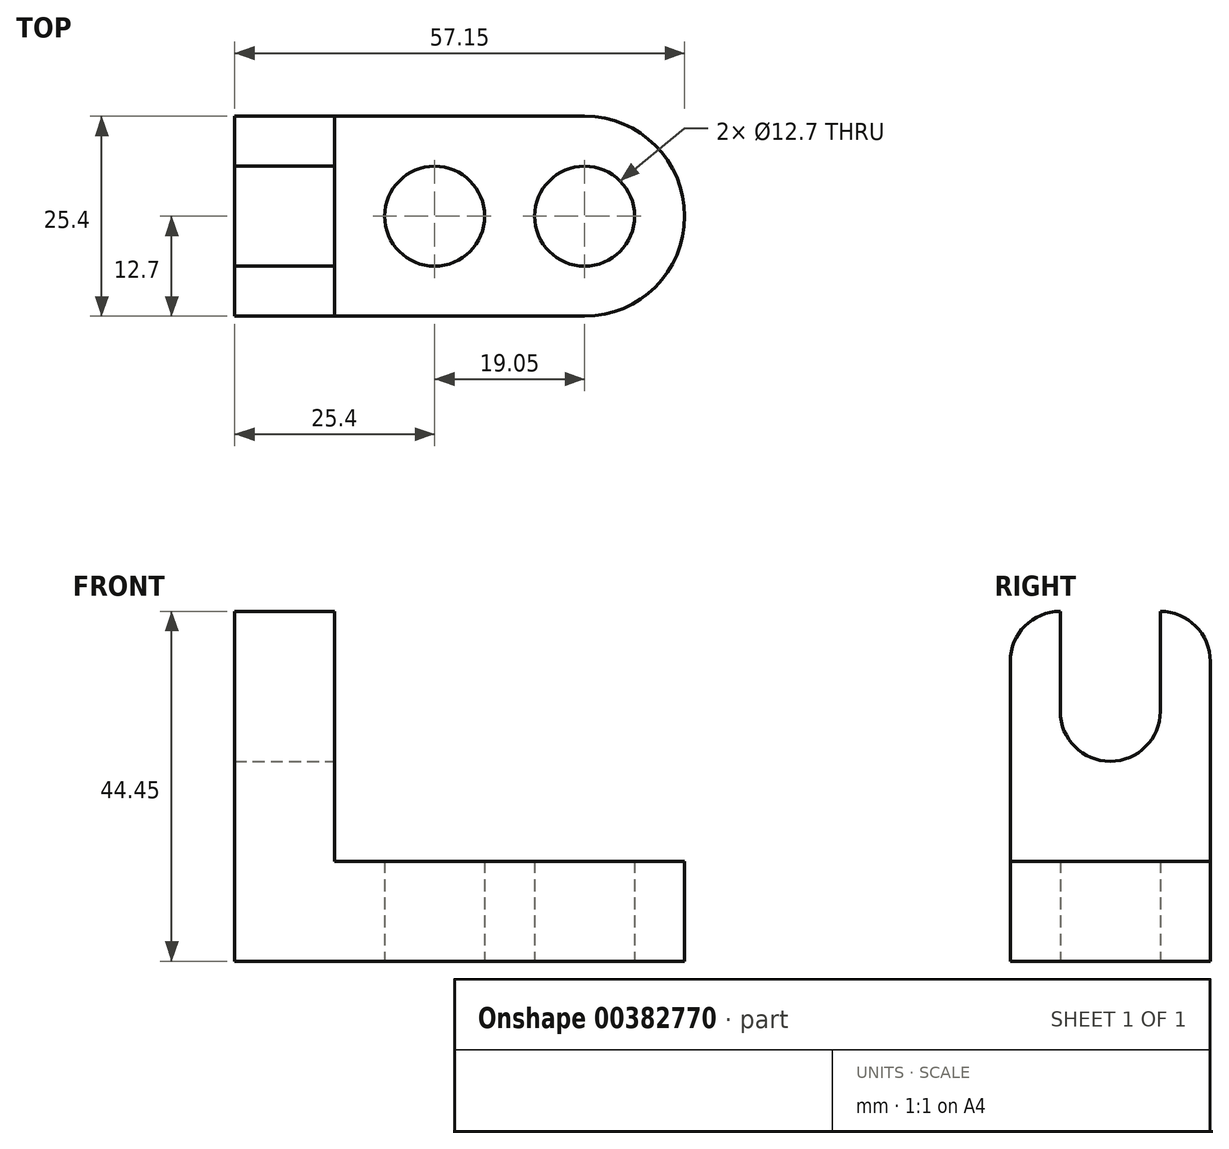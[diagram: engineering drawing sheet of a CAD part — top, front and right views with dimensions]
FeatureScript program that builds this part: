
annotation { "Feature Type Name" : "Feature", "Feature Type Description" : "" }
export const myFeature = defineFeature(function(context is Context, id is Id, definition is map)
    precondition{}
    {
        {
            var Q0;
            Q0=qCreatedBy(makeId("Front.planeOp"),FACE);
            var sketch = newSketch(context, id + "F0", { "sketchPlane" : qUnion([Q0])});
            skLineSegment(sketch, "E0", {"start": v(0, 0) * mm, "end": v(-57.15, 0) * mm});
            skLineSegment(sketch, "E1", {"start": v(-57.15, 0) * mm, "end": v(-57.15, 44.45) * mm});
            skLineSegment(sketch, "E2", {"start": v(-57.15, 44.45) * mm, "end": v(-44.45, 44.45) * mm});
            skLineSegment(sketch, "E3", {"start": v(-44.45, 44.45) * mm, "end": v(-44.45, 12.7) * mm});
            skLineSegment(sketch, "E4", {"start": v(-44.45, 12.7) * mm, "end": v(0, 12.7) * mm});
            skLineSegment(sketch, "E5", {"start": v(0, 12.7) * mm, "end": v(0, 0) * mm});
            skSolve(sketch);
        }
        {
            var Q0;
            Q0 = qSketchRegion(id + "F0", true);
            extrude(context, id + "F1", {"entities" : qUnion([Q0]), "depth" : 25.4 * mm});
        }
        {
            var Q0;
            Q0=qCreatedBy(makeId("Top.planeOp"),FACE);
            var sketch = newSketch(context, id + "F2", { "sketchPlane" : qUnion([Q0])});
            skCircle(sketch, "E6", {"center": v(-31.75, -12.7) * mm, "radius": 6.35 * mm});
            skCircle(sketch, "E7", {"center": v(-12.7, -12.7) * mm, "radius": 6.35 * mm});
            skArc(sketch, "E8", {"start": v(0, -12.7) * mm, "mid": v(-3.72, -3.72) * mm, "end": v(-12.7, 0) * mm});
            skArc(sketch, "E9", {"start": v(-12.7, -25.4) * mm, "mid": v(-3.72, -21.68) * mm, "end": v(0, -12.7) * mm});
            skLineSegment(sketch, "E10", {"start": v(-12.7, 0) * mm, "end": v(0, 0) * mm});
            skLineSegment(sketch, "E11", {"start": v(0, 0) * mm, "end": v(0, -12.7) * mm});
            skLineSegment(sketch, "E12", {"start": v(0, -12.7) * mm, "end": v(0, -25.4) * mm});
            skLineSegment(sketch, "E13", {"start": v(0, -25.4) * mm, "end": v(-12.7, -25.4) * mm});
            skSolve(sketch);
        }
        {
            var Q0;
            Q0 = qSketchRegion(id + "F2", true);
            extrude(context, id + "F3", {"entities" : qUnion([Q0]), "operationType" : NewBodyOperationType.REMOVE, "depth" : 25.4 * mm});
        }
        {
            var Q0;
            Q0=makeQuery(id+"F1.opExtrude","SWEPT_FACE",FACE,{"disambiguationData":[OSD([sQuery(id+"F0.wireOp",EDGE,"E3")])]});
            var sketch = newSketch(context, id + "F4", { "sketchPlane" : qUnion([Q0])});
            skLineSegment(sketch, "E14", {"start": v(-6.35, 44.45) * mm, "end": v(-19.05, 44.45) * mm});
            skLineSegment(sketch, "E15", {"start": v(-19.05, 44.45) * mm, "end": v(-19.05, 12.7) * mm});
            skLineSegment(sketch, "E16", {"start": v(-19.05, 12.7) * mm, "end": v(-6.35, 12.7) * mm});
            skLineSegment(sketch, "E17", {"start": v(-6.35, 12.7) * mm, "end": v(-6.35, 44.45) * mm});
            skArc(sketch, "E18", {"start": v(-19.05, 31.75) * mm, "mid": v(-12.7, 25.4) * mm, "end": v(-6.35, 31.75) * mm});
            skSolve(sketch);
        }
        {
            var Q0;
            {var subQ0=sQuery(id+"F4.wireOp",EDGE,"E14");Q0=makeQuery(id+"F4.imprint","IMPRINT",FACE,{"disambiguationData":[TD([[makeQuery(id+"F4.imprint","IMPRINT",EDGE,{"derivedFrom":subQ0}),-1.0]])]});}
            extrude(context, id + "F5", {"entities" : qUnion([Q0]), "operationType" : NewBodyOperationType.REMOVE, "oppositeDirection" : true, "depth" : 25.4 * mm});
        }
        {
            var Q0;
            Q0=makeQuery(id+"F1.opExtrude","SWEPT_FACE",FACE,{"disambiguationData":[OSD([sQuery(id+"F0.wireOp",EDGE,"E3")])]});
            var sketch = newSketch(context, id + "F6", { "sketchPlane" : qUnion([Q0])});
            skArc(sketch, "E19", {"start": v(-19.05, 44.45) * mm, "mid": v(-23.54, 42.6) * mm, "end": v(-25.4, 38.1) * mm});
            skArc(sketch, "E20", {"start": v(0, 38.1) * mm, "mid": v(-1.86, 42.6) * mm, "end": v(-6.35, 44.45) * mm});
            skLineSegment(sketch, "E21", {"start": v(-25.4, 38.1) * mm, "end": v(-25.4, 44.45) * mm});
            skLineSegment(sketch, "E22", {"start": v(-25.4, 44.45) * mm, "end": v(-19.05, 44.45) * mm});
            skLineSegment(sketch, "E23", {"start": v(-6.35, 44.45) * mm, "end": v(0, 44.45) * mm});
            skLineSegment(sketch, "E24", {"start": v(0, 44.45) * mm, "end": v(0, 38.1) * mm});
            skSolve(sketch);
        }
        {
            var Q0;
            Q0 = qSketchRegion(id + "F6", true);
            extrude(context, id + "F7", {"entities" : qUnion([Q0]), "operationType" : NewBodyOperationType.REMOVE, "oppositeDirection" : true, "depth" : 25.4 * mm});
        }
    });
